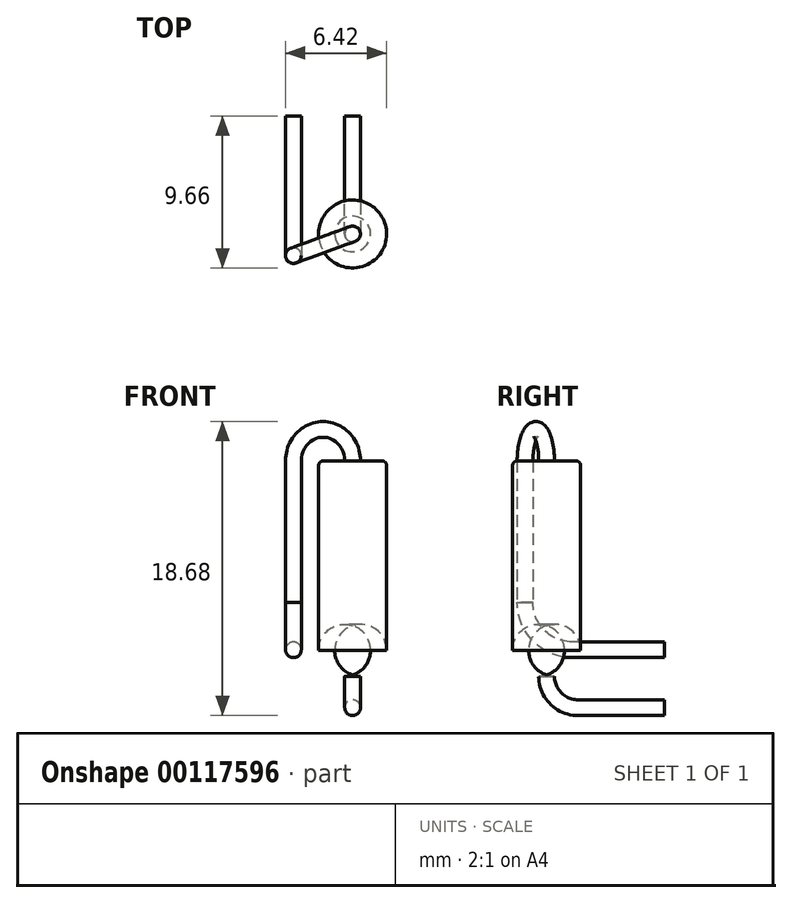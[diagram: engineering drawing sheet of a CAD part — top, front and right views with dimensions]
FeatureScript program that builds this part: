
annotation { "Feature Type Name" : "Feature", "Feature Type Description" : "" }
export const myFeature = defineFeature(function(context is Context, id is Id, definition is map)
    precondition{}
    {
        {
            var Q0;
            Q0=qCreatedBy(makeId("Top.planeOp"),FACE);
            var sketch = newSketch(context, id + "F0", { "sketchPlane" : qUnion([Q0])});
            skCircle(sketch, "E0", {"center": v(0, 0) * mm, "radius": 2.16 * mm});
            skSolve(sketch);
        }
        {
            var Q0;
            Q0=makeQuery(id+"F0.imprint","IMPRINT",FACE,{"disambiguationData":[TD([[makeQuery(id+"F0.imprint","IMPRINT",EDGE,{"derivedFrom":sQuery(id+"F0.wireOp",EDGE,"E0")}),1.0]])]});
            extrude(context, id + "F1", {"entities" : qUnion([Q0]), "depth" : 13.68 * mm});
        }
        {
            var Q0;
            Q0=makeQuery(id+"F1.opExtrude","CAP_EDGE",EDGE,{"disambiguationData":[OSD([sQuery(id+"F0.wireOp",EDGE,"E0")])],"isStart":true});
            fillet(context, id + "F2", {"entities" : qUnion([Q0]), "radius" : 1.65 * mm, "tangentPropagation" : true, "allowEdgeOverflow" : false});
        }
        {
            var Q0;
            Q0=makeQuery(id+"F1.opExtrude","CAP_FACE",FACE,{"disambiguationData":[OSD([sQuery(id+"F0.wireOp",EDGE,"E0")])],"isStart":true});
            var sketch = newSketch(context, id + "F3", { "sketchPlane" : qUnion([Q0])});
            skCircle(sketch, "E1", {"center": v(0, 0) * mm, "radius": 0.5 * mm});
            skSolve(sketch);
        }
        {
            var Q0;
            Q0=makeQuery(id+"F1.opExtrude","CAP_EDGE",EDGE,{"disambiguationData":[OSD([sQuery(id+"F0.wireOp",EDGE,"E0")])],"isStart":false});
            fillet(context, id + "F4", {"entities" : qUnion([Q0]), "radius" : 0.3 * mm, "tangentPropagation" : true, "allowEdgeOverflow" : false});
        }
        {
            var Q0;
            Q0=makeQuery(id+"F1.opExtrude","CAP_FACE",FACE,{"disambiguationData":[OSD([sQuery(id+"F0.wireOp",EDGE,"E0")])],"isStart":false});
            var sketch = newSketch(context, id + "F5", { "sketchPlane" : qUnion([Q0])});
            skCircle(sketch, "E2", {"center": v(0, 0) * mm, "radius": 0.5 * mm});
            skSolve(sketch);
        }
        {
            var Q0;
            Q0=qCreatedBy(makeId("Front.planeOp"),FACE);
            var sketch = newSketch(context, id + "F6", { "sketchPlane" : qUnion([Q0])});
            skArc(sketch, "E3", {"start": v(0, 13.68) * mm, "mid": v(-2, 15.68) * mm, "end": v(-4, 13.68) * mm});
            skLineSegment(sketch, "E4", {"start": v(-4, 13.68) * mm, "end": v(-4, 4.68) * mm});
            skLineSegment(sketch, "E5", {"start": v(0, 13.68) * mm, "end": v(-4, 13.68) * mm, "construction": true});
            skLineSegment(sketch, "E6", {"start": v(0, 13.68) * mm, "end": v(0, 0) * mm, "construction": true});
            skSolve(sketch);
        }
        {
            var Q0;
            Q0=makeQuery(id+"F5.imprint","IMPRINT",FACE,{"disambiguationData":[TD([[makeQuery(id+"F5.imprint","IMPRINT",EDGE,{"derivedFrom":sQuery(id+"F5.wireOp",EDGE,"E2")}),1.0]])]});
            var Q1;
            Q1=sQuery(id+"F6.wireOp",EDGE,"E3");
            var Q2;
            Q2=sQuery(id+"F6.wireOp",EDGE,"E4");
            sweep(context, id + "F7", {"profiles" : qUnion([Q0]), "path" : qUnion([Q1, Q2])});
        }
        {
            var Q0;
            Q0=qCreatedBy(makeId("Right.planeOp"),FACE);
            var sketch = newSketch(context, id + "F8", { "sketchPlane" : qUnion([Q0])});
            skArc(sketch, "E7", {"start": v(0, 0) * mm, "mid": v(0.59, -1.41) * mm, "end": v(2, -2) * mm});
            skLineSegment(sketch, "E8", {"start": v(2, -2) * mm, "end": v(7.5, -2) * mm});
            skSolve(sketch);
        }
        {
            var Q0;
            Q0=makeQuery(id+"F3.imprint","IMPRINT",FACE,{"disambiguationData":[TD([[makeQuery(id+"F3.imprint","IMPRINT",EDGE,{"derivedFrom":sQuery(id+"F3.wireOp",EDGE,"E1")}),1.0]])]});
            var Q1;
            Q1 = qConstructionFilter(qBodyType(qCreatedBy(id + "F8" ,EDGE), BodyType.WIRE), ConstructionObject.NO);
            sweep(context, id + "F9", {"operationType" : NewBodyOperationType.ADD, "profiles" : qUnion([Q0]), "path" : qUnion([Q1])});
        }
        {
            var Q0;
            Q0=qCreatedBy(makeId("Right.planeOp"),FACE);
            cPlane(context, id + "F10", {"entities" : qUnion([Q0]), "cplaneType" : CPlaneType.OFFSET, "offset" : 5.08 * mm, "oppositeDirection" : true, "width" : 150 * mm, "height" : 150 * mm});
        }
        {
            var Q0;
            Q0=qCreatedBy(id+"F10.planeOp",FACE);
            var sketch = newSketch(context, id + "F11", { "sketchPlane" : qUnion([Q0])});
            skLineSegment(sketch, "E9", {"start": v(0, 4.68) * mm, "end": v(0, 1.68) * mm, "construction": true});
            skArc(sketch, "E10", {"start": v(0, 4.68) * mm, "mid": v(0.88, 2.56) * mm, "end": v(3, 1.68) * mm});
            skSolve(sketch);
        }
        {
            var Q0;
            Q0=makeQuery(id+"F7.opSweep","CAP_FACE",FACE,{"disambiguationData":[OSD([sQuery(id+"F5.wireOp",EDGE,"E2"),sQuery(id+"F6.wireOp",VERTEX,"E4.end")])],"isStart":false});
            var Q1;
            Q1=makeQuery(id+"F7.opSweep","CAP_EDGE",EDGE,{"disambiguationData":[OSD([sQuery(id+"F5.wireOp",EDGE,"E2"),sQuery(id+"F6.wireOp",VERTEX,"E4.end")])],"isStart":false});
            var Q2;
            Q2 = qConstructionFilter(qBodyType(qCreatedBy(id + "F11" ,EDGE), BodyType.WIRE), ConstructionObject.NO);
            sweep(context, id + "F12", {"profiles" : qUnion([Q0]), "surfaceProfiles" : qUnion([Q1]), "path" : qUnion([Q2])});
        }
        {
            var Q0;
            Q0=makeQuery(id+"F12.opSweep","SWEPT_BODY",BODY,{"disambiguationData":[OSD([sQuery(id+"F5.wireOp",EDGE,"E2"),sQuery(id+"F6.wireOp",VERTEX,"E4.end"),sQuery(id+"F11.wireOp",EDGE,"qxFlNoGR-Y62T-Z2I8-TnkK-WULOVYEd25lG")])]});
            var Q1;
            Q1=sQuery(id+"F6.wireOp",EDGE,"E4");
            transform(context, id + "F13", {"entities" : qUnion([Q0]), "transformType" : TransformType.ROTATION, "transformAxis" : qUnion([Q1]), "angle" : 20 * degree, "makeCopy" : false});
        }
        {
            var Q0;
            Q0=makeQuery(id+"F7.opSweep","SWEPT_BODY",BODY,{"disambiguationData":[OSD([sQuery(id+"F5.wireOp",EDGE,"E2"),sQuery(id+"F6.wireOp",EDGE,"E4")])]});
            var Q1;
            Q1=makeQuery(id+"F12.opSweep","SWEPT_BODY",BODY,{"disambiguationData":[OSD([sQuery(id+"F5.wireOp",EDGE,"E2"),sQuery(id+"F6.wireOp",VERTEX,"E4.end"),sQuery(id+"F11.wireOp",EDGE,"qxFlNoGR-Y62T-Z2I8-TnkK-WULOVYEd25lG")])]});
            var Q2;
            Q2=sQuery(id+"F6.wireOp",EDGE,"E6");
            transform(context, id + "F14", {"entities" : qUnion([Q0, Q1]), "transformType" : TransformType.ROTATION, "transformAxis" : qUnion([Q2]), "angle" : 20 * degree, "oppositeDirection" : true, "makeCopy" : false});
        }
        {
            var Q0;
            Q0=makeQuery(id+"F12.opSweep","CAP_FACE",FACE,{"disambiguationData":[OSD([sQuery(id+"F5.wireOp",EDGE,"E2"),sQuery(id+"F6.wireOp",VERTEX,"E4.end"),sQuery(id+"F11.wireOp",VERTEX,"E10.end")])],"isStart":false});
            var Q1;
            Q1=makeQuery(id+"F9.opSweep","CAP_FACE",FACE,{"disambiguationData":[OSD([sQuery(id+"F3.wireOp",EDGE,"E1"),sQuery(id+"F8.wireOp",VERTEX,"E8.end")])],"isStart":false});
            extrude(context, id + "F15", {"entities" : qUnion([Q0]), "operationType" : NewBodyOperationType.ADD, "endBound" : BoundingType.UP_TO_SURFACE, "endBoundEntityFace" : qUnion([Q1]), "depth" : 25 * mm});
        }
    });
